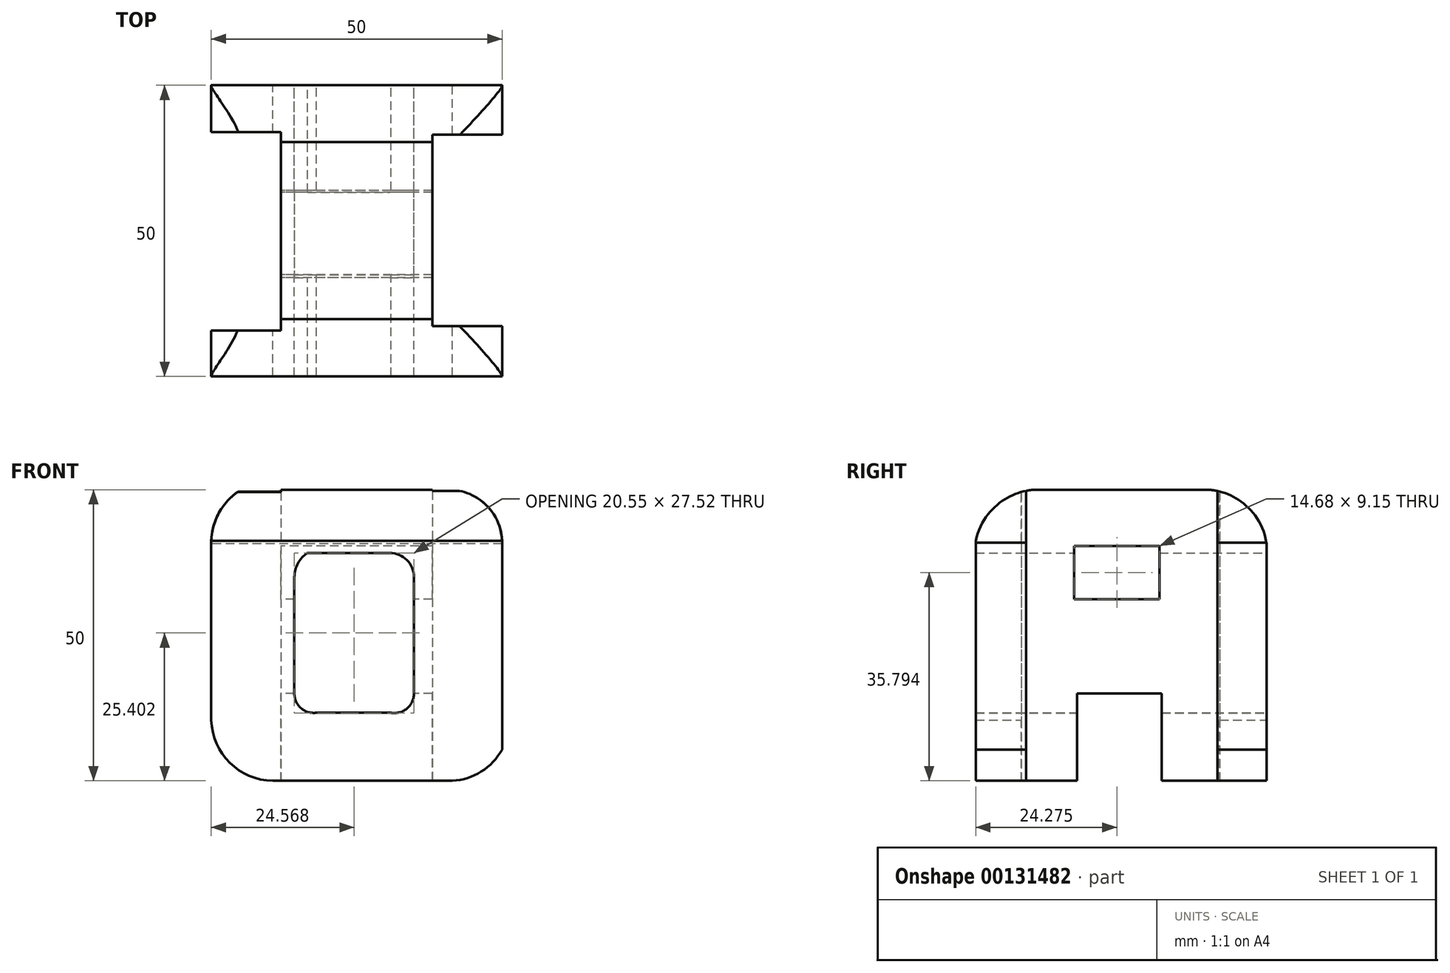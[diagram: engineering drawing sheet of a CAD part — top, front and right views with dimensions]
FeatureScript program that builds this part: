
annotation { "Feature Type Name" : "Feature", "Feature Type Description" : "" }
export const myFeature = defineFeature(function(context is Context, id is Id, definition is map)
    precondition{}
    {
        {
            var Q0;
            Q0=qCreatedBy(makeId("Top.planeOp"),FACE);
            var sketch = newSketch(context, id + "F0", { "sketchPlane" : qUnion([Q0])});
            skLineSegment(sketch, "E0.bottom", {"start": v(-25, 25) * mm, "end": v(25, 25) * mm});
            skLineSegment(sketch, "E0.top", {"start": v(-25, -25) * mm, "end": v(25, -25) * mm});
            skLineSegment(sketch, "E0.left", {"start": v(-25, 25) * mm, "end": v(-25, 16.94) * mm});
            skLineSegment(sketch, "E0.right", {"start": v(25, 25) * mm, "end": v(25, 16.54) * mm});
            skPoint(sketch, "E0.middle", {"position": v(0, 0) * mm});
            skLineSegment(sketch, "E1", {"start": v(25, 16.54) * mm, "end": v(13, 16.54) * mm});
            skLineSegment(sketch, "E2", {"start": v(25, 25) * mm, "end": v(-25, 25) * mm});
            skLineSegment(sketch, "E3", {"start": v(-25, 16.94) * mm, "end": v(-13, 16.94) * mm});
            skLineSegment(sketch, "E4", {"start": v(-13, 16.94) * mm, "end": v(-13, -17.14) * mm});
            skLineSegment(sketch, "E5", {"start": v(13, 16.54) * mm, "end": v(13, -16.34) * mm});
            skLineSegment(sketch, "E6", {"start": v(13, -16.34) * mm, "end": v(25, -16.34) * mm});
            skLineSegment(sketch, "E7", {"start": v(25, -16.34) * mm, "end": v(25, -25) * mm});
            skLineSegment(sketch, "E8", {"start": v(25, -25) * mm, "end": v(-25, -25) * mm});
            skLineSegment(sketch, "E9", {"start": v(-25, -25) * mm, "end": v(-25, -17.14) * mm});
            skLineSegment(sketch, "E10", {"start": v(-25, -17.14) * mm, "end": v(-13, -17.14) * mm});
            skLineSegment(sketch, "E11", {"start": v(-25, 16.94) * mm, "end": v(-25, 25) * mm});
            skLineSegment(sketch, "E12", {"start": v(25, 16.54) * mm, "end": v(25, 25) * mm});
            skLineSegment(sketch, "E13.trimOffspring", {"start": v(-25, -17.14) * mm, "end": v(-25, -25) * mm});
            skSolve(sketch);
        }
        {
            var Q0;
            Q0=qCreatedBy(makeId("Front.planeOp"),FACE);
            var sketch = newSketch(context, id + "F1", { "sketchPlane" : qUnion([Q0])});
            skLineSegment(sketch, "E14.bottom", {"start": v(-19.9, 25) * mm, "end": v(15.85, 25) * mm});
            skLineSegment(sketch, "E14.top", {"start": v(-14.07, -25) * mm, "end": v(15.27, -25) * mm});
            skLineSegment(sketch, "E14.left", {"start": v(-25, -13.9) * mm, "end": v(-25, -14.57) * mm});
            skLineSegment(sketch, "E14.right", {"start": v(25, -9.52) * mm, "end": v(25, -19.61) * mm});
            skPoint(sketch, "E14.middle", {"position": v(0, 0) * mm});
            skLineSegment(sketch, "E15", {"start": v(15.85, 25) * mm, "end": v(-19.9, 25) * mm});
            skArc(sketch, "E16", {"start": v(-19.9, 25) * mm, "mid": v(-23.66, 21.04) * mm, "end": v(-25, 15.75) * mm});
            skArc(sketch, "E17", {"start": v(25, 15.95) * mm, "mid": v(22.28, 22.35) * mm, "end": v(15.85, 25) * mm});
            skArc(sketch, "E18", {"start": v(-25, -14.57) * mm, "mid": v(-21.67, -22.02) * mm, "end": v(-14.07, -25) * mm});
            skArc(sketch, "E19", {"start": v(15.27, -25) * mm, "mid": v(20.91, -23.7) * mm, "end": v(25, -19.61) * mm});
            skPoint(sketch, "E20.orphan", {"position": v(25, 25) * mm});
            skPoint(sketch, "E21.orphan", {"position": v(25, -25) * mm});
            skPoint(sketch, "E22.orphan", {"position": v(-25, -25) * mm});
            skPoint(sketch, "E23.orphan", {"position": v(-25, 25) * mm});
            skLineSegment(sketch, "E24", {"start": v(25, 15.95) * mm, "end": v(25, -19.61) * mm});
            skLineSegment(sketch, "E25", {"start": v(-25, 15.75) * mm, "end": v(-25, -14.57) * mm});
            skLineSegment(sketch, "E26", {"start": v(-10.7, 0) * mm, "end": v(-10.7, 10.02) * mm});
            skLineSegment(sketch, "E27", {"start": v(-10.7, 0) * mm, "end": v(-10.7, -10.02) * mm});
            skLineSegment(sketch, "E28", {"start": v(9.84, 0) * mm, "end": v(9.84, 10.02) * mm});
            skLineSegment(sketch, "E29", {"start": v(9.84, 0) * mm, "end": v(9.84, -10.02) * mm});
            skLineSegment(sketch, "E30", {"start": v(-6.9, -13.3) * mm, "end": v(5.87, -13.3) * mm});
            skLineSegment(sketch, "E31", {"start": v(-8.46, 14.16) * mm, "end": v(4.32, 14.16) * mm});
            skLineSegment(sketch, "E32", {"start": v(4.32, 14.16) * mm, "end": v(5.7, 14.16) * mm});
            skArc(sketch, "E33", {"start": v(5.87, -13.3) * mm, "mid": v(8.63, -12.6) * mm, "end": v(9.84, -10.02) * mm});
            skArc(sketch, "E34", {"start": v(-10.7, -10.02) * mm, "mid": v(-9.56, -12.53) * mm, "end": v(-6.9, -13.3) * mm});
            skArc(sketch, "E35", {"start": v(-8.46, 14.16) * mm, "mid": v(-10.1, 12.37) * mm, "end": v(-10.7, 10.02) * mm});
            skArc(sketch, "E36", {"start": v(9.84, 10.02) * mm, "mid": v(8.63, 12.95) * mm, "end": v(5.7, 14.16) * mm});
            skSolve(sketch);
        }
        {
            var Q0;
            Q0=qCreatedBy(makeId("Right.planeOp"),FACE);
            var sketch = newSketch(context, id + "F2", { "sketchPlane" : qUnion([Q0])});
            skPoint(sketch, "E37.middle", {"position": v(0, 0) * mm});
            skLineSegment(sketch, "E38", {"start": v(-7.55, -25) * mm, "end": v(-7.55, -10.02) * mm});
            skLineSegment(sketch, "E39", {"start": v(-7.55, -10.02) * mm, "end": v(6.96, -10.02) * mm});
            skLineSegment(sketch, "E40", {"start": v(6.96, -10.02) * mm, "end": v(6.96, -25) * mm});
            skLineSegment(sketch, "E41", {"start": v(-8.06, 6.22) * mm, "end": v(6.61, 6.22) * mm});
            skLineSegment(sketch, "E42", {"start": v(6.61, 6.22) * mm, "end": v(6.61, 15.37) * mm});
            skLineSegment(sketch, "E43", {"start": v(6.61, 15.37) * mm, "end": v(-8.06, 15.37) * mm});
            skLineSegment(sketch, "E44", {"start": v(-8.06, 15.37) * mm, "end": v(-8.06, 6.22) * mm});
            skArc(sketch, "E45", {"start": v(-15.15, 25) * mm, "mid": v(-21.51, 22.23) * mm, "end": v(-25, 16.23) * mm});
            skArc(sketch, "E46", {"start": v(25, 15.72) * mm, "mid": v(21.73, 22.05) * mm, "end": v(15.25, 25) * mm});
            skPoint(sketch, "E47.orphan", {"position": v(-25, 25) * mm});
            skPoint(sketch, "E48.orphan", {"position": v(25, -25) * mm});
            skPoint(sketch, "E49.orphan", {"position": v(-25, -25) * mm});
            skLineSegment(sketch, "E50", {"start": v(-25, 16.23) * mm, "end": v(-25, -25) * mm});
            skLineSegment(sketch, "E51", {"start": v(-25, -25) * mm, "end": v(-7.55, -25) * mm});
            skLineSegment(sketch, "E52", {"start": v(6.96, -25) * mm, "end": v(25, -25) * mm});
            skLineSegment(sketch, "E53", {"start": v(25, -25) * mm, "end": v(25, 15.72) * mm});
            skLineSegment(sketch, "E54", {"start": v(-15.15, 25) * mm, "end": v(15.25, 25) * mm});
            skPoint(sketch, "E37.right.start.orphan", {"position": v(25, 25) * mm});
            skSolve(sketch);
        }
        {
            var Q0;
            Q0 = qSketchRegion(id + "F1", true);
            extrude(context, id + "F3", {"entities" : qUnion([Q0]), "endBound" : BoundingType.SYMMETRIC, "depth" : 50 * mm});
        }
        {
            var Q0;
            Q0 = qSketchRegion(id + "F2", true);
            extrude(context, id + "F4", {"entities" : qUnion([Q0]), "operationType" : NewBodyOperationType.INTERSECT, "endBound" : BoundingType.SYMMETRIC, "depth" : 50 * mm});
        }
        {
            var Q0;
            Q0 = qSketchRegion(id + "F0", true);
            extrude(context, id + "F5", {"entities" : qUnion([Q0]), "operationType" : NewBodyOperationType.INTERSECT, "endBound" : BoundingType.SYMMETRIC, "depth" : 50 * mm});
        }
    });
